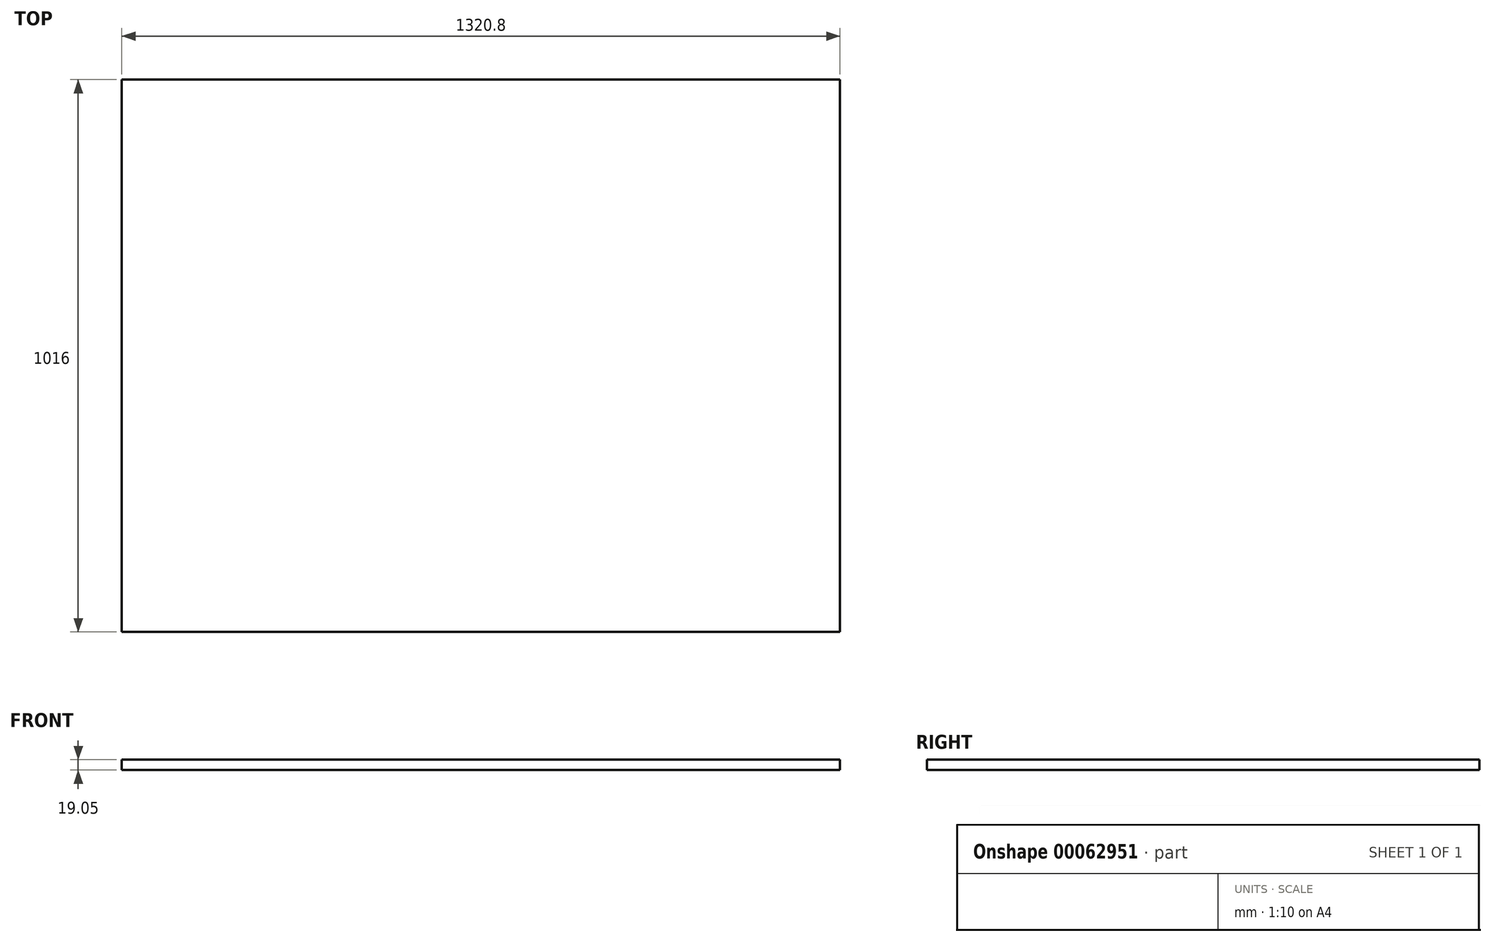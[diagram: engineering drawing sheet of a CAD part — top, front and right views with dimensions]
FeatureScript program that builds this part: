
annotation { "Feature Type Name" : "Feature", "Feature Type Description" : "" }
export const myFeature = defineFeature(function(context is Context, id is Id, definition is map)
    precondition{}
    {
        {
            var Q0;
            Q0=qCreatedBy(makeId("Top.planeOp"),FACE);
            var sketch = newSketch(context, id + "F0", { "sketchPlane" : qUnion([Q0])});
            skLineSegment(sketch, "E0.rect.bottom", {"start": v(-660.4, 508) * mm, "end": v(660.4, 508) * mm});
            skLineSegment(sketch, "E0.rect.top", {"start": v(-660.4, -508) * mm, "end": v(660.4, -508) * mm});
            skLineSegment(sketch, "E0.rect.left", {"start": v(-660.4, 508) * mm, "end": v(-660.4, -508) * mm});
            skLineSegment(sketch, "E0.rect.right", {"start": v(660.4, 508) * mm, "end": v(660.4, -508) * mm});
            skPoint(sketch, "E0.rect.middle", {"position": v(0, 0) * mm});
            skSolve(sketch);
        }
        {
            var Q0;
            Q0=makeQuery(id+"F0.imprint","IMPRINT",FACE,{"disambiguationData":[TD([[makeQuery(id+"F0.imprint","IMPRINT",EDGE,{"derivedFrom":sQuery(id+"F0.wireOp",EDGE,"E0.rect.bottom")}),-1.0]])]});
            extrude(context, id + "F1", {"entities" : qUnion([Q0]), "depth" : 19.05 * mm});
        }
    });
